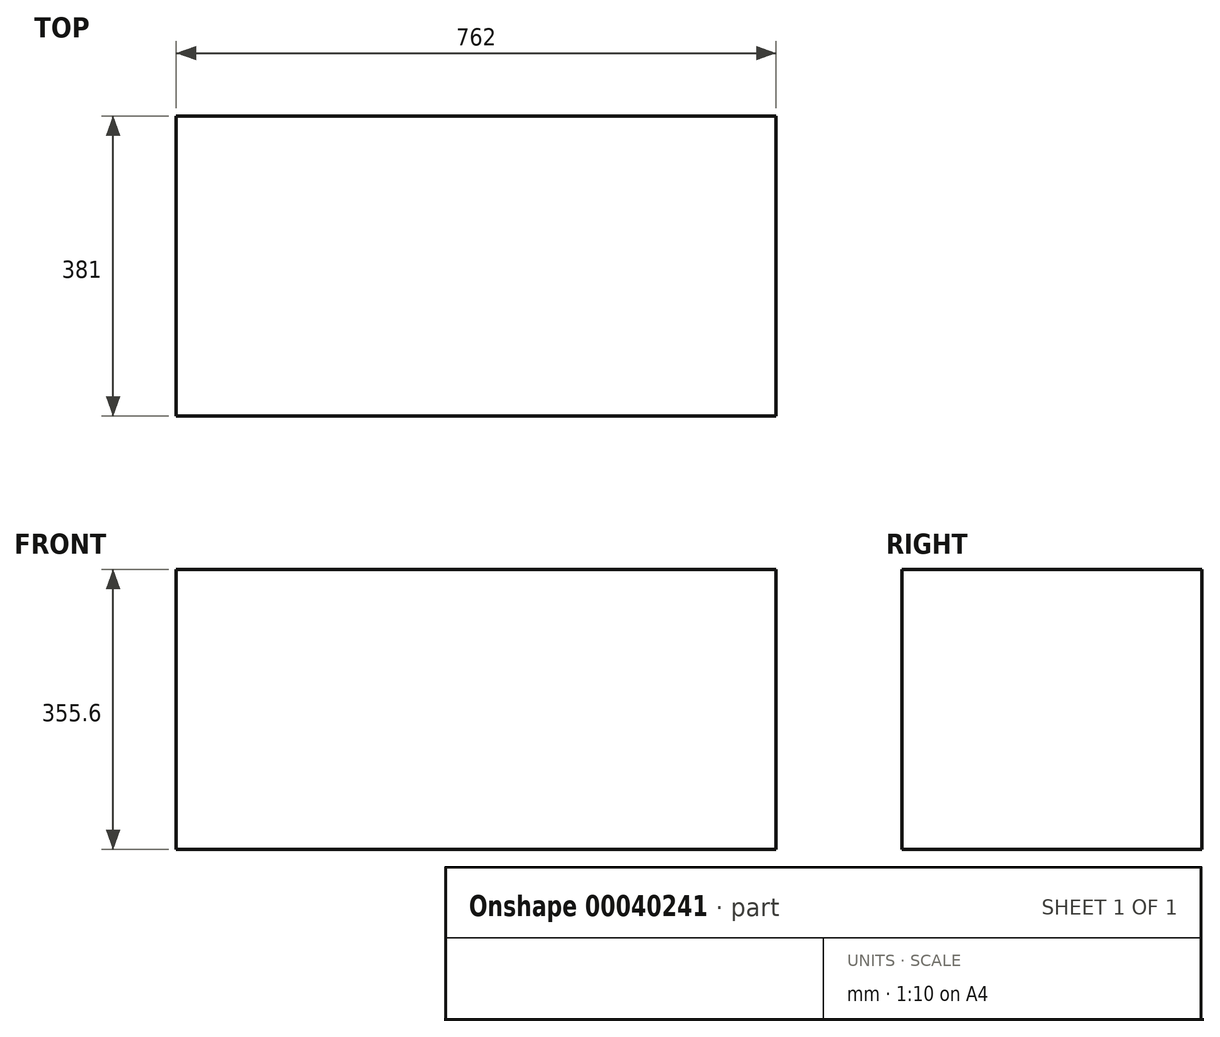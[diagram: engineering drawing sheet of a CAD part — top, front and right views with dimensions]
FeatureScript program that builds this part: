
annotation { "Feature Type Name" : "Feature", "Feature Type Description" : "" }
export const myFeature = defineFeature(function(context is Context, id is Id, definition is map)
    precondition{}
    {
        {
            var Q0;
            Q0=qCreatedBy(makeId("Front.planeOp"),FACE);
            var sketch = newSketch(context, id + "F0", { "sketchPlane" : qUnion([Q0])});
            skLineSegment(sketch, "E0.rect.bottom", {"start": v(381, 177.8) * mm, "end": v(-381, 177.8) * mm});
            skLineSegment(sketch, "E0.rect.top", {"start": v(381, -177.8) * mm, "end": v(-381, -177.8) * mm});
            skLineSegment(sketch, "E0.rect.left", {"start": v(381, 177.8) * mm, "end": v(381, -177.8) * mm});
            skLineSegment(sketch, "E0.rect.right", {"start": v(-381, 177.8) * mm, "end": v(-381, -177.8) * mm});
            skPoint(sketch, "E0.rect.middle", {"position": v(0, 0) * mm});
            skSolve(sketch);
        }
        {
            var Q0;
            Q0=qSketchRegion(id+"F0",true);
            extrude(context, id + "F1", {"entities" : qUnion([Q0]), "endBound" : BoundingType.SYMMETRIC, "depth" : 381 * mm});
        }
    });
